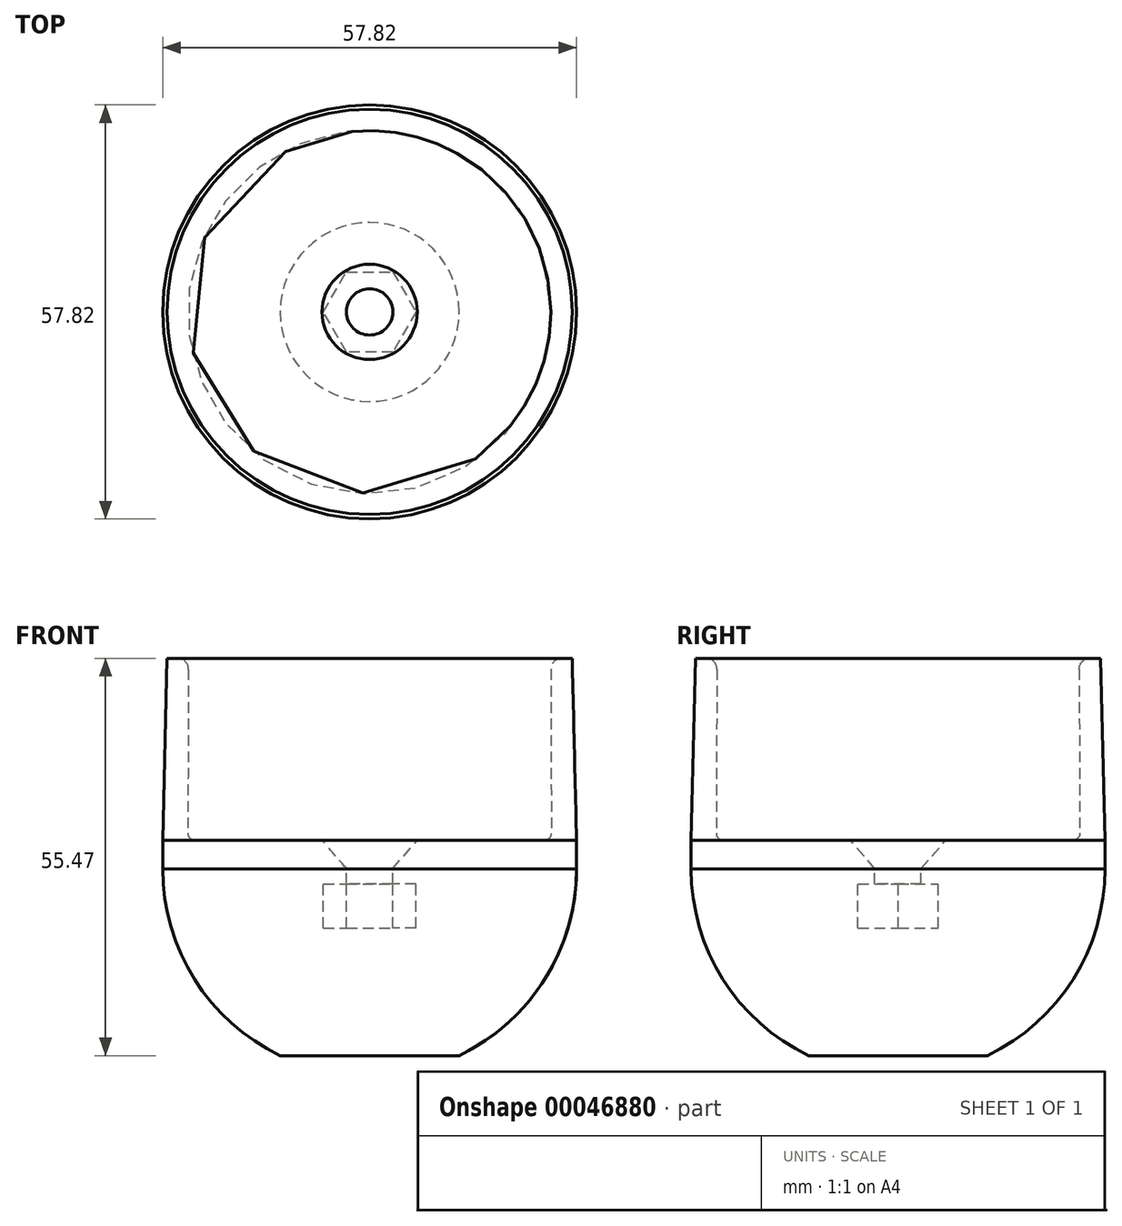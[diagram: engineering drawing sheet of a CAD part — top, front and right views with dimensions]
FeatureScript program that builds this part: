
annotation { "Feature Type Name" : "Feature", "Feature Type Description" : "" }
export const myFeature = defineFeature(function(context is Context, id is Id, definition is map)
    precondition{}
    {
        {
            var Q0;
            Q0=qCreatedBy(makeId("Front.planeOp"),FACE);
            var sketch = newSketch(context, id + "F0", { "sketchPlane" : qUnion([Q0])});
            skLineSegment(sketch, "E0", {"start": v(0, 0) * mm, "end": v(-25.4, 0) * mm});
            skLineSegment(sketch, "E1", {"start": v(-25.4, 0) * mm, "end": v(-25.3, 25.4) * mm});
            skLineSegment(sketch, "E2", {"start": v(-25.3, 25.4) * mm, "end": v(-28.3, 25.4) * mm});
            skLineSegment(sketch, "E3", {"start": v(-28.3, 25.4) * mm, "end": v(-28.9, 0) * mm});
            skLineSegment(sketch, "E4", {"start": v(0, 0) * mm, "end": v(0, -4) * mm});
            skLineSegment(sketch, "E5", {"start": v(0, -4) * mm, "end": v(-28.9, -4) * mm});
            skLineSegment(sketch, "E6", {"start": v(-28.9, -4) * mm, "end": v(-28.9, 0) * mm});
            skSolve(sketch);
        }
        {
            var Q0;
            Q0=qSketchRegion(id+"F0",true);
            var Q1;
            Q1=sQuery(id+"F0.wireOp",EDGE,"E4");
            revolve(context, id + "F1", {"entities" : qUnion([Q0]), "axis" : qUnion([Q1]), "revolveType" : RevolveType.FULL});
        }
        {
            var Q0;
            Q0=makeQuery(id+"F1.opRevolve","SWEPT_EDGE",EDGE,{"disambiguationData":[OSD([sQuery(id+"F0.wireOp",EDGE,"E0"),sQuery(id+"F0.wireOp",EDGE,"E1")])]});
            fillet(context, id + "F2", {"entities" : qUnion([Q0]), "radius" : 1 * mm, "allowEdgeOverflow" : false});
        }
        {
            var Q0;
            Q0=makeQuery(id+"F1.opRevolve","SWEPT_EDGE",EDGE,{"disambiguationData":[OSD([sQuery(id+"F0.wireOp",EDGE,"E1"),sQuery(id+"F0.wireOp",EDGE,"E2")])]});
            fillet(context, id + "F3", {"entities" : qUnion([Q0]), "radius" : 1.5 * mm, "allowEdgeOverflow" : false});
        }
        {
            var Q0;
            Q0=makeQuery(id+"F1.opRevolve","SWEPT_FACE",FACE,{"disambiguationData":[OSD([sQuery(id+"F0.wireOp",EDGE,"E2")])]});
            var sketch = newSketch(context, id + "F4", { "sketchPlane" : qUnion([Q0])});
            skLineSegment(sketch, "E7.bottom", {"start": v(-2.5, 32.82) * mm, "end": v(2.5, 32.82) * mm});
            skLineSegment(sketch, "E7.top", {"start": v(-2.5, 0) * mm, "end": v(2.5, 0) * mm});
            skLineSegment(sketch, "E7.left", {"start": v(-2.5, 32.82) * mm, "end": v(-2.5, 0) * mm});
            skLineSegment(sketch, "E7.right", {"start": v(2.5, 32.82) * mm, "end": v(2.5, 0) * mm});
            skLineSegment(sketch, "E8.1.0", {"start": v(-29.67, -14.25) * mm, "end": v(-1.25, 2.17) * mm});
            skLineSegment(sketch, "E8.1.1", {"start": v(-27.17, -18.58) * mm, "end": v(1.25, -2.17) * mm});
            skLineSegment(sketch, "E8.1.2", {"start": v(1.25, -2.17) * mm, "end": v(-1.25, 2.17) * mm});
            skLineSegment(sketch, "E8.1.3", {"start": v(-27.17, -18.58) * mm, "end": v(-29.67, -14.25) * mm});
            skLineSegment(sketch, "E8.2.0", {"start": v(27.17, -18.58) * mm, "end": v(-1.25, -2.17) * mm});
            skLineSegment(sketch, "E8.2.1", {"start": v(29.67, -14.25) * mm, "end": v(1.25, 2.17) * mm});
            skLineSegment(sketch, "E8.2.2", {"start": v(1.25, 2.17) * mm, "end": v(-1.25, -2.17) * mm});
            skLineSegment(sketch, "E8.2.3", {"start": v(29.67, -14.25) * mm, "end": v(27.17, -18.58) * mm});
            skPoint(sketch, "E8.center", {"position": v(0, 0) * mm});
            skSolve(sketch);
        }
        {
            var Q0;
            Q0=qCreatedBy(makeId("Front.planeOp"),FACE);
            var sketch = newSketch(context, id + "F5", { "sketchPlane" : qUnion([Q0])});
            skLineSegment(sketch, "E9", {"start": v(0, 11.3) * mm, "end": v(0, -15.68) * mm});
            skLineSegment(sketch, "E10", {"start": v(0, -15.68) * mm, "end": v(-3.17, -15.68) * mm});
            skLineSegment(sketch, "E11", {"start": v(-3.17, -15.68) * mm, "end": v(-3.17, -4) * mm, "construction": true});
            skLineSegment(sketch, "E12", {"start": v(-3.17, -4) * mm, "end": v(-6.65, -4) * mm, "construction": true});
            skLineSegment(sketch, "E13", {"start": v(-6.65, 11.3) * mm, "end": v(0, 11.3) * mm});
            skLineSegment(sketch, "E14", {"start": v(-3.17, -4) * mm, "end": v(-6.65, 0) * mm});
            skLineSegment(sketch, "E15", {"start": v(-6.65, 0) * mm, "end": v(0, 0) * mm});
            skLineSegment(sketch, "E16", {"start": v(-6.65, 11.3) * mm, "end": v(-6.65, 0) * mm});
            skLineSegment(sketch, "E17", {"start": v(-6.65, -4) * mm, "end": v(-6.65, 0) * mm, "construction": true});
            skLineSegment(sketch, "E18", {"start": v(-3.24, -15.68) * mm, "end": v(-3.24, -3.93) * mm});
            skLineSegment(sketch, "E19", {"start": v(0, -15.68) * mm, "end": v(-3.24, -15.68) * mm});
            skSolve(sketch);
        }
        {
            var Q0;
            Q0=qSketchRegion(id+"F5",true);
            var Q1;
            Q1=sQuery(id+"F5.wireOp",EDGE,"E9");
            revolve(context, id + "F6", {"operationType" : NewBodyOperationType.REMOVE, "entities" : qUnion([Q0]), "axis" : qUnion([Q1]), "revolveType" : RevolveType.FULL, "oppositeDirection" : true});
        }
        {
            var Q0;
            Q0=qCreatedBy(makeId("Front.planeOp"),FACE);
            var sketch = newSketch(context, id + "F7", { "sketchPlane" : qUnion([Q0])});
            skLineSegment(sketch, "E20.0", {"start": v(-28.9, -4) * mm, "end": v(0, -4) * mm});
            skLineSegment(sketch, "E21", {"start": v(0, -4) * mm, "end": v(28.9, -4) * mm, "construction": true});
            skLineSegment(sketch, "E22", {"start": v(0, -4) * mm, "end": v(0, -30.07) * mm});
            skArc(sketch, "E23", {"start": v(-28.9, -4) * mm, "mid": v(-24.46, -19.4) * mm, "end": v(-12.5, -30.07) * mm});
            skLineSegment(sketch, "E24", {"start": v(0, -30.07) * mm, "end": v(-12.5, -30.07) * mm});
            skArc(sketch, "E25", {"start": v(-12.5, -30.07) * mm, "mid": v(-6.4, -32.19) * mm, "end": v(0, -32.9) * mm, "construction": true});
            skLineSegment(sketch, "E26", {"start": v(0, -30.07) * mm, "end": v(0, -32.9) * mm, "construction": true});
            skSolve(sketch);
        }
        {
            var Q0;
            Q0=qSketchRegion(id+"F7",true);
            var Q1;
            Q1=sQuery(id+"F7.wireOp",EDGE,"E22");
            revolve(context, id + "F8", {"entities" : qUnion([Q0]), "axis" : qUnion([Q1]), "revolveType" : RevolveType.FULL});
        }
        {
            var Q0;
            Q0=makeQuery(id+"F8.opRevolve","SWEPT_FACE",FACE,{"disambiguationData":[OSD([sQuery(id+"F7.wireOp",EDGE,"E20.0")])]});
            var sketch = newSketch(context, id + "F9", { "sketchPlane" : qUnion([Q0])});
            skCircle(sketch, "E27.cCircle", {"center": v(0, 0) * mm, "radius": 5.6 * mm, "construction": true});
            skLineSegment(sketch, "E27.0", {"start": v(-3.23, 5.6) * mm, "end": v(3.23, 5.6) * mm});
            skLineSegment(sketch, "E27.1", {"start": v(3.23, 5.6) * mm, "end": v(6.47, 0) * mm});
            skLineSegment(sketch, "E27.2", {"start": v(6.47, 0) * mm, "end": v(3.23, -5.6) * mm});
            skLineSegment(sketch, "E27.3", {"start": v(3.23, -5.6) * mm, "end": v(-3.23, -5.6) * mm});
            skLineSegment(sketch, "E27.4", {"start": v(-3.23, -5.6) * mm, "end": v(-6.47, 0) * mm});
            skLineSegment(sketch, "E27.5", {"start": v(-6.47, 0) * mm, "end": v(-3.23, 5.6) * mm});
            skPoint(sketch, "E27.0.midPoint", {"position": v(0, 5.6) * mm});
            skSolve(sketch);
        }
        {
            var Q0;
            Q0=qSketchRegion(id+"F9",true);
            extrude(context, id + "F10", {"entities" : qUnion([Q0]), "oppositeDirection" : true, "depth" : 6.2 * mm});
        }
        {
            var Q0;
            Q0=makeQuery(id+"F10.opExtrude","SWEPT_BODY",BODY,{"disambiguationData":[OSD([sQuery(id+"F9.wireOp",EDGE,"E27.0"),sQuery(id+"F9.wireOp",EDGE,"E27.1"),sQuery(id+"F9.wireOp",EDGE,"E27.2"),sQuery(id+"F9.wireOp",EDGE,"E27.3"),sQuery(id+"F9.wireOp",EDGE,"E27.4"),sQuery(id+"F9.wireOp",EDGE,"E27.5")])]});
            var Q1;
            Q1=makeQuery(id+"F8.opRevolve","SWEPT_FACE",FACE,{"disambiguationData":[OSD([sQuery(id+"F7.wireOp",EDGE,"E20.0")])]});
            transform(context, id + "F11", {"entities" : qUnion([Q0]), "transformType" : TransformType.TRANSLATION_DISTANCE, "transformDirection" : qUnion([Q1]), "distance" : 2.06 * mm, "oppositeDirection" : true, "makeCopy" : false});
        }
        {
            var Q0;
            Q0=makeQuery(id+"F10.opExtrude","SWEPT_BODY",BODY,{"disambiguationData":[OSD([sQuery(id+"F9.wireOp",EDGE,"E27.0"),sQuery(id+"F9.wireOp",EDGE,"E27.1"),sQuery(id+"F9.wireOp",EDGE,"E27.2"),sQuery(id+"F9.wireOp",EDGE,"E27.3"),sQuery(id+"F9.wireOp",EDGE,"E27.4"),sQuery(id+"F9.wireOp",EDGE,"E27.5")])]});
            var Q1;
            Q1=makeQuery(id+"F8.opRevolve","SWEPT_BODY",BODY,{"disambiguationData":[OSD([sQuery(id+"F7.wireOp",EDGE,"E20.0"),sQuery(id+"F7.wireOp",EDGE,"E22"),sQuery(id+"F7.wireOp",EDGE,"E23"),sQuery(id+"F7.wireOp",EDGE,"E24")])]});
            booleanBodies(context, id + "F12", {"operationType" : BooleanOperationType.SUBTRACTION, "tools" : qUnion([Q0]), "targets" : qUnion([Q1])});
        }
        {
            var Q0;
            Q0=makeQuery(id+"F8.opRevolve","SWEPT_FACE",FACE,{"disambiguationData":[OSD([sQuery(id+"F7.wireOp",EDGE,"E20.0")])]});
            var sketch = newSketch(context, id + "F13", { "sketchPlane" : qUnion([Q0])});
            skCircle(sketch, "E28.0", {"center": v(0, 0) * mm, "radius": 3.24 * mm});
            skSolve(sketch);
        }
        {
            var Q0;
            Q0=qSketchRegion(id+"F13",true);
            extrude(context, id + "F14", {"entities" : qUnion([Q0]), "operationType" : NewBodyOperationType.REMOVE, "oppositeDirection" : true, "depth" : 2.06 * mm});
        }
    });
